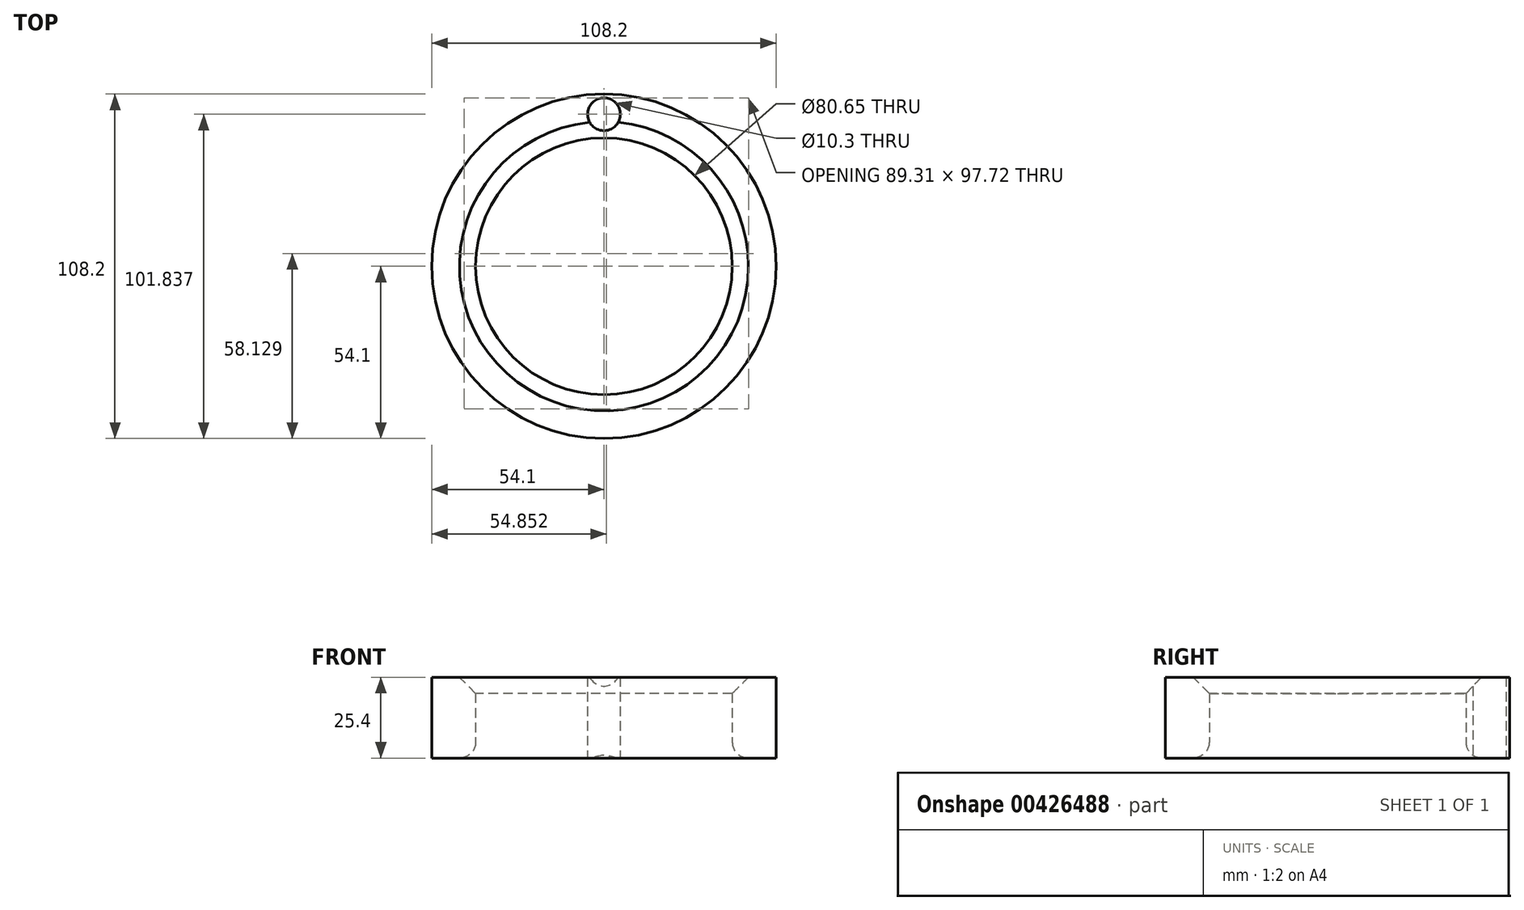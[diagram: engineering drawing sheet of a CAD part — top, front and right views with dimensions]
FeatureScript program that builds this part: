
annotation { "Feature Type Name" : "Feature", "Feature Type Description" : "" }
export const myFeature = defineFeature(function(context is Context, id is Id, definition is map)
    precondition{}
    {
        {
            var Q0;
            Q0=qCreatedBy(makeId("Top.planeOp"),FACE);
            var sketch = newSketch(context, id + "F0", { "sketchPlane" : qUnion([Q0])});
            skCircle(sketch, "E0", {"center": v(0, 0) * mm, "radius": 54.1 * mm});
            skCircle(sketch, "E1", {"center": v(0, 0) * mm, "radius": 40.33 * mm});
            skSolve(sketch);
        }
        {
            var Q0;
            Q0=makeQuery(id+"F0.imprint","IMPRINT",FACE,{"disambiguationData":[TD([[makeQuery(id+"F0.imprint","IMPRINT",EDGE,{"derivedFrom":sQuery(id+"F0.wireOp",EDGE,"E0")}),1.0]])]});
            extrude(context, id + "F1", {"entities" : qUnion([Q0]), "depth" : 25.4 * mm, "offsetDistance" : 25.4 * mm});
        }
        {
            var Q0;
            Q0=qCreatedBy(makeId("Top.planeOp"),FACE);
            var sketch = newSketch(context, id + "F2", { "sketchPlane" : qUnion([Q0])});
            skCircle(sketch, "E2", {"center": v(0, 47.74) * mm, "radius": 5.15 * mm});
            skSolve(sketch);
        }
        {
            var Q0;
            Q0 = qSketchRegion(id + "F2", true);
            extrude(context, id + "F3", {"entities" : qUnion([Q0]), "operationType" : NewBodyOperationType.REMOVE, "endBound" : BoundingType.THROUGH_ALL, "depth" : 15 * mm, "offsetDistance" : 25.4 * mm});
        }
        {
            var Q0;
            Q0=makeQuery(id+"F1.opExtrude","CAP_EDGE",EDGE,{"disambiguationData":[OSD([sQuery(id+"F0.wireOp",EDGE,"E1")])],"isStart":false});
            chamfer(context, id + "F4", {"entities" : qUnion([Q0]), "width" : 5.08 * mm, "tangentPropagation" : true});
        }
        {
            var Q0;
            Q0=makeQuery(id+"F1.opExtrude","CAP_EDGE",EDGE,{"disambiguationData":[OSD([sQuery(id+"F0.wireOp",EDGE,"E1")])],"isStart":true});
            fillet(context, id + "F5", {"entities" : qUnion([Q0]), "radius" : 5.08 * mm, "tangentPropagation" : true, "allowEdgeOverflow" : false});
        }
    });
